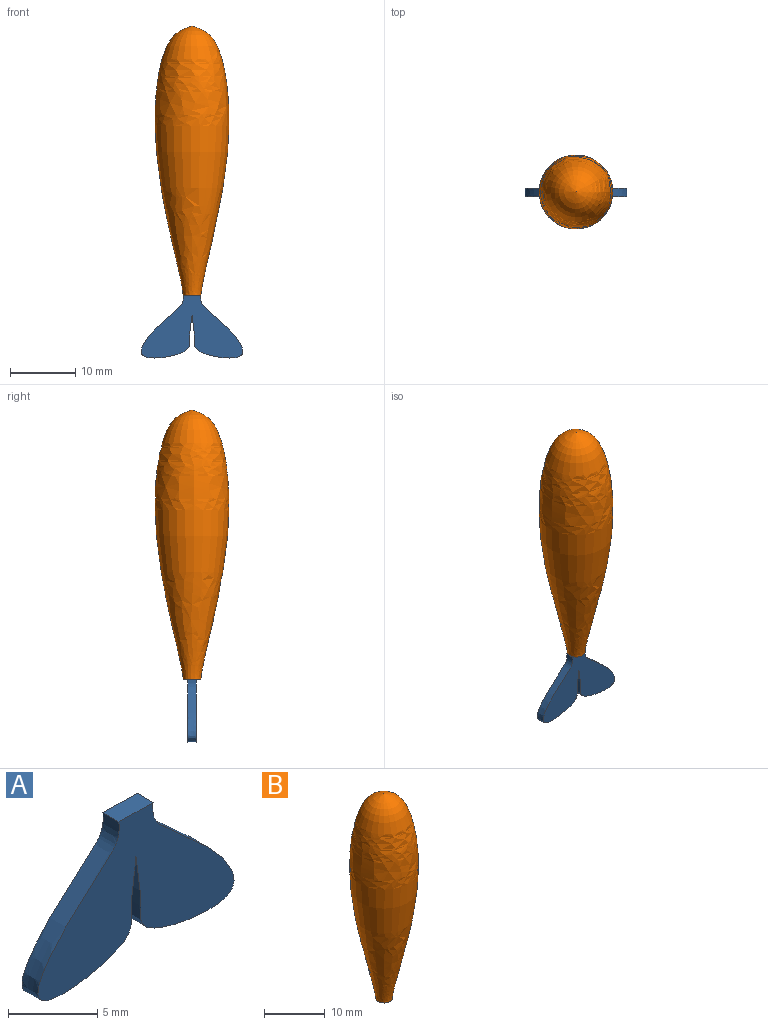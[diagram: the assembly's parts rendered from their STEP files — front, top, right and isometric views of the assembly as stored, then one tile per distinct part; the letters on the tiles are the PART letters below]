
ASSEMBLY  parts=2 mates=1
PART A: 5 faces, bbox 16.1x1.3x10.2 mm
  f0: extruded ~9.58x7.76mm, area 30.7mm2, adj f1,f2,f3,f4
  f1: extruded ~9.58x7.76mm, area 30.7mm2, adj f0,f2,f3,f4
  f2: plane 2.7x1.27mm, normal (0,0,1), area 3.4mm2, adj f0,f1,f3,f4
  f3: plane 16.15x10.19mm, normal (0,-1,0), area 83.9mm2, adj f0,f1,f2
  f4: plane 16.15x10.19mm, normal (0,1,0), area 83.9mm2, adj f0,f1,f2
PART B: 2 faces, bbox 11.3x11.3x41.3 mm
  f0: revolved ~41.28x11.34mm, area 1115.4mm2, adj f1
  f1: plane 2.7x2.7mm, normal (0,0,-1), area 5.7mm2, adj f0
PLACE A t=(1.01,0.52,2.08)mm
PLACE B t=(1.01,0.52,35.23)mm
MATE fastened A.f2 <-> B.f1  axis (0,0,1) through (1.01,0.52,-6.05)mm
